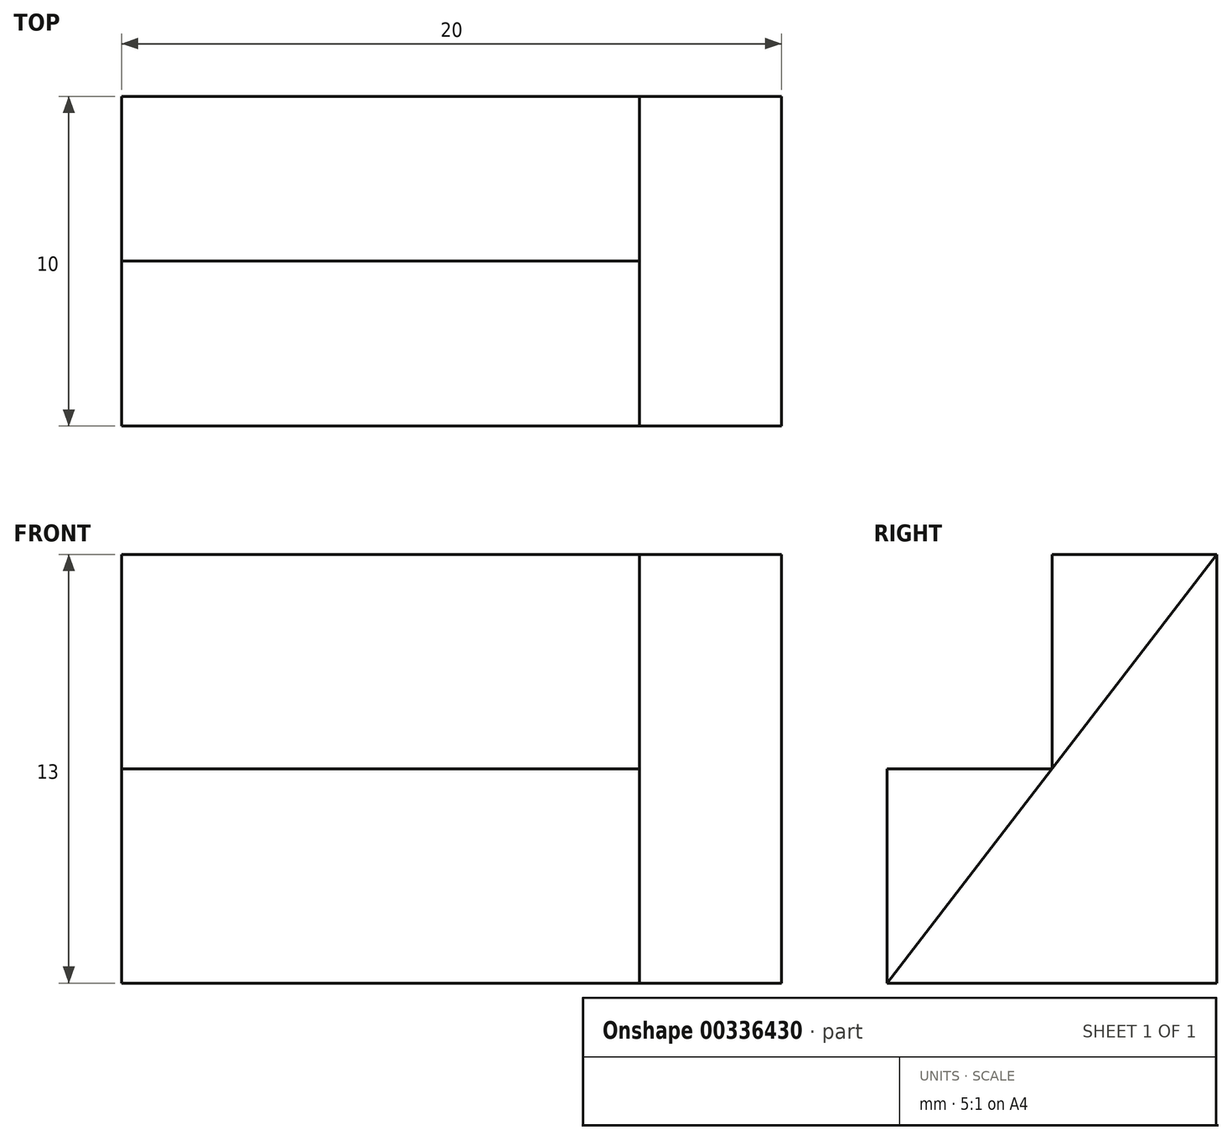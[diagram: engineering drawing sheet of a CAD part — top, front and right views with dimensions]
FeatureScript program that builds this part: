
annotation { "Feature Type Name" : "Feature", "Feature Type Description" : "" }
export const myFeature = defineFeature(function(context is Context, id is Id, definition is map)
    precondition{}
    {
        {
            var Q0;
            Q0=qCreatedBy(makeId("Top.planeOp"),FACE);
            var sketch = newSketch(context, id + "F0", { "sketchPlane" : qUnion([Q0])});
            skLineSegment(sketch, "E0.bottom", {"start": v(0, 0) * mm, "end": v(20, 0) * mm});
            skLineSegment(sketch, "E0.top", {"start": v(0, 10) * mm, "end": v(20, 10) * mm});
            skLineSegment(sketch, "E0.left", {"start": v(0, 0) * mm, "end": v(0, 10) * mm});
            skLineSegment(sketch, "E0.right", {"start": v(20, 0) * mm, "end": v(20, 10) * mm});
            skSolve(sketch);
        }
        {
            var Q0;
            Q0 = qSketchRegion(id + "F0", true);
            extrude(context, id + "F1", {"entities" : qUnion([Q0]), "depth" : 13 * mm});
        }
        {
            var Q0;
            Q0=makeQuery(id+"F1.opExtrude","SWEPT_FACE",FACE,{"disambiguationData":[OSD([sQuery(id+"F0.wireOp",EDGE,"E0.right")])]});
            var sketch = newSketch(context, id + "F2", { "sketchPlane" : qUnion([Q0])});
            skLineSegment(sketch, "E1", {"start": v(0, 0) * mm, "end": v(10, 13) * mm});
            skLineSegment(sketch, "E2", {"start": v(10, 13) * mm, "end": v(0, 13) * mm});
            skLineSegment(sketch, "E3", {"start": v(0, 13) * mm, "end": v(0, 0) * mm});
            skSolve(sketch);
        }
        {
            var Q0;
            Q0 = qSketchRegion(id + "F2", true);
            extrude(context, id + "F3", {"entities" : qUnion([Q0]), "operationType" : NewBodyOperationType.REMOVE, "oppositeDirection" : true, "depth" : 4.3 * mm});
        }
        {
            var Q0;
            Q0=makeQuery(id+"F1.opExtrude","SWEPT_FACE",FACE,{"disambiguationData":[OSD([sQuery(id+"F0.wireOp",EDGE,"E0.left")])]});
            var sketch = newSketch(context, id + "F4", { "sketchPlane" : qUnion([Q0])});
            skLineSegment(sketch, "E4", {"start": v(-5, 13) * mm, "end": v(-5, 6.5) * mm});
            skLineSegment(sketch, "E5", {"start": v(-5, 6.5) * mm, "end": v(0, 6.5) * mm});
            skLineSegment(sketch, "E6", {"start": v(0, 6.5) * mm, "end": v(0, 13) * mm});
            skLineSegment(sketch, "E7", {"start": v(0, 13) * mm, "end": v(-5, 13) * mm});
            skSolve(sketch);
        }
        {
            var Q0;
            Q0 = qSketchRegion(id + "F4", true);
            extrude(context, id + "F5", {"entities" : qUnion([Q0]), "operationType" : NewBodyOperationType.REMOVE, "oppositeDirection" : true, "depth" : 15.8 * mm});
        }
    });
